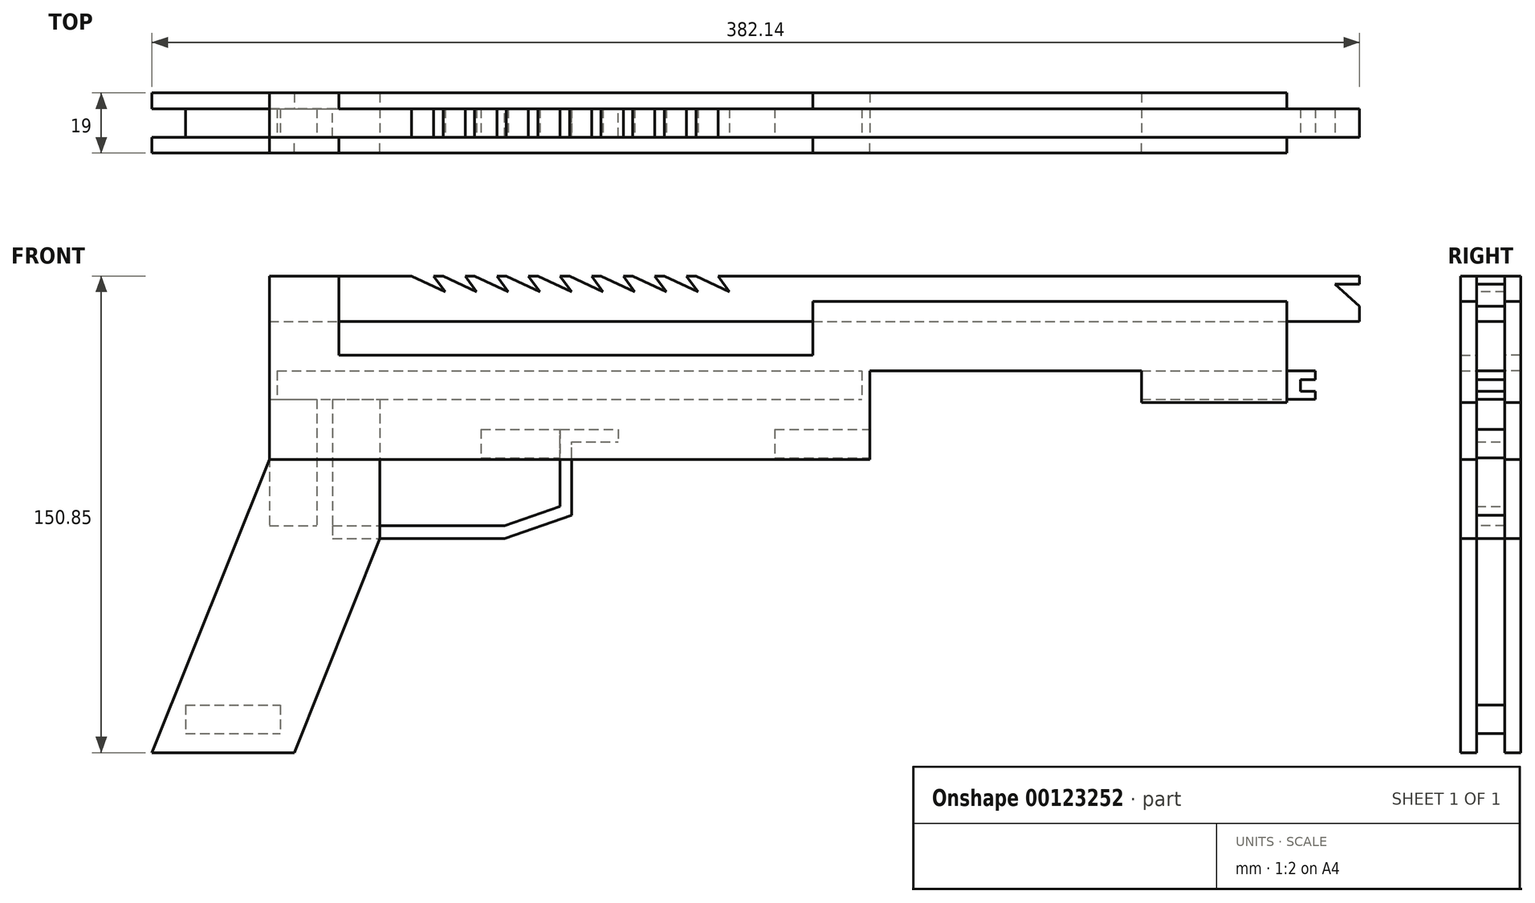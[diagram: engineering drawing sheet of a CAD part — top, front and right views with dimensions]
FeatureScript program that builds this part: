
annotation { "Feature Type Name" : "Feature", "Feature Type Description" : "" }
export const myFeature = defineFeature(function(context is Context, id is Id, definition is map)
    precondition{}
    {
        {
            var Q0;
            Q0=qCreatedBy(makeId("Front.planeOp"),FACE);
            cPlane(context, id + "F0", {"entities" : qUnion([Q0]), "cplaneType" : CPlaneType.OFFSET, "offset" : 4.5 * mm, "oppositeDirection" : true, "width" : 150 * mm, "height" : 150 * mm});
        }
        {
            var Q0;
            Q0=qCreatedBy(id+"F0.planeOp",FACE);
            var sketch = newSketch(context, id + "F1", { "sketchPlane" : qUnion([Q0])});
            skLineSegment(sketch, "E0", {"start": v(0, 0) * mm, "end": v(22, 0) * mm});
            skLineSegment(sketch, "E1", {"start": v(22, 0) * mm, "end": v(22, -25) * mm});
            skLineSegment(sketch, "E2", {"start": v(22, -25) * mm, "end": v(172, -25) * mm});
            skLineSegment(sketch, "E3", {"start": v(172, -25) * mm, "end": v(172, -8) * mm});
            skLineSegment(sketch, "E4", {"start": v(172, -8) * mm, "end": v(322, -8) * mm});
            skLineSegment(sketch, "E5", {"start": v(322, -8) * mm, "end": v(322, -40) * mm});
            skLineSegment(sketch, "E6", {"start": v(322, -40) * mm, "end": v(276, -40) * mm});
            skLineSegment(sketch, "E7", {"start": v(276, -40) * mm, "end": v(276, -30) * mm});
            skLineSegment(sketch, "E8", {"start": v(276, -30) * mm, "end": v(190, -30) * mm});
            skLineSegment(sketch, "E9", {"start": v(190, -30) * mm, "end": v(190, -58) * mm});
            skLineSegment(sketch, "E10", {"start": v(190, -58) * mm, "end": v(0, -58) * mm});
            skLineSegment(sketch, "E11", {"start": v(0, -58) * mm, "end": v(0, 0) * mm});
            skSolve(sketch);
        }
        {
            var Q0;
            Q0=makeQuery(id+"F1.imprint","IMPRINT",FACE,{"disambiguationData":[TD([[makeQuery(id+"F1.imprint","IMPRINT",EDGE,{"derivedFrom":sQuery(id+"F1.wireOp",EDGE,"E0")}),-1.0]])]});
            extrude(context, id + "F2", {"entities" : qUnion([Q0]), "oppositeDirection" : true, "depth" : 5 * mm});
        }
        {
            var Q0;
            Q0=qCreatedBy(makeId("Front.planeOp"),FACE);
            var sketch = newSketch(context, id + "F3", { "sketchPlane" : qUnion([Q0])});
            skLineSegment(sketch, "E12.bottom", {"start": v(2.5, -30) * mm, "end": v(187.5, -30) * mm});
            skLineSegment(sketch, "E12.top", {"start": v(2.5, -39) * mm, "end": v(187.5, -39) * mm});
            skLineSegment(sketch, "E12.left", {"start": v(2.5, -30) * mm, "end": v(2.5, -39) * mm});
            skLineSegment(sketch, "E12.right", {"start": v(187.5, -30) * mm, "end": v(187.5, -39) * mm});
            skLineSegment(sketch, "E13.bottom", {"start": v(276, -30) * mm, "end": v(331, -30) * mm});
            skLineSegment(sketch, "E13.top", {"start": v(276, -39) * mm, "end": v(331, -39) * mm});
            skLineSegment(sketch, "E13.left", {"start": v(276, -30) * mm, "end": v(276, -39) * mm});
            skLineSegment(sketch, "E13.right", {"start": v(331, -30) * mm, "end": v(331, -32.76) * mm});
            skLineSegment(sketch, "E14", {"start": v(331, -32.76) * mm, "end": v(326.28, -32.76) * mm});
            skLineSegment(sketch, "E15", {"start": v(326.28, -32.76) * mm, "end": v(326.28, -36.44) * mm});
            skLineSegment(sketch, "E16", {"start": v(326.28, -36.44) * mm, "end": v(331, -36.44) * mm});
            skLineSegment(sketch, "E17.trimOffspring", {"start": v(331, -36.44) * mm, "end": v(331, -39) * mm});
            skSolve(sketch);
        }
        {
            var Q0;
            Q0 = qSketchRegion(id + "F3", true);
            extrude(context, id + "F4", {"entities" : qUnion([Q0]), "operationType" : NewBodyOperationType.ADD, "endBound" : BoundingType.SYMMETRIC, "oppositeDirection" : true, "depth" : 9 * mm});
        }
        {
            var Q0;
            Q0=qCreatedBy(makeId("Front.planeOp"),FACE);
            var sketch = newSketch(context, id + "F5", { "sketchPlane" : qUnion([Q0])});
            skLineSegment(sketch, "E18.bottom", {"start": v(0, 0) * mm, "end": v(45, 0) * mm});
            skLineSegment(sketch, "E18.top", {"start": v(41.55, -5) * mm, "end": v(41.69, -5) * mm});
            skLineSegment(sketch, "E18.left", {"start": v(0, 0) * mm, "end": v(0, -5) * mm});
            skLineSegment(sketch, "E19.bottom", {"start": v(40.03, 0) * mm, "end": v(39.9, 0) * mm});
            skLineSegment(sketch, "E19.top", {"start": v(41.69, -5) * mm, "end": v(41.55, -5) * mm});
            skLineSegment(sketch, "E20.bottom", {"start": v(55, 0) * mm, "end": v(52.02, 0) * mm});
            skLineSegment(sketch, "E21", {"start": v(45, 0) * mm, "end": v(55.63, -5) * mm});
            skLineSegment(sketch, "E22", {"start": v(55.63, -5) * mm, "end": v(52.02, 0) * mm});
            skLineSegment(sketch, "E23", {"start": v(52.02, 0) * mm, "end": v(55, 0) * mm});
            skLineSegment(sketch, "E24.1.0.0", {"start": v(55, 0) * mm, "end": v(65.63, -5) * mm});
            skLineSegment(sketch, "E24.1.0.1", {"start": v(65.63, -5) * mm, "end": v(62.02, 0) * mm});
            skLineSegment(sketch, "E24.2.0.0", {"start": v(65, 0) * mm, "end": v(75.63, -5) * mm});
            skLineSegment(sketch, "E24.2.0.1", {"start": v(75.63, -5) * mm, "end": v(72.02, 0) * mm});
            skLineSegment(sketch, "E24.3.0.0", {"start": v(75, 0) * mm, "end": v(85.63, -5) * mm});
            skLineSegment(sketch, "E24.3.0.1", {"start": v(85.63, -5) * mm, "end": v(82.02, 0) * mm});
            skLineSegment(sketch, "E24.4.0.0", {"start": v(85, 0) * mm, "end": v(95.63, -5) * mm});
            skLineSegment(sketch, "E24.4.0.1", {"start": v(95.63, -5) * mm, "end": v(92.02, 0) * mm});
            skLineSegment(sketch, "E24.5.0.0", {"start": v(95, 0) * mm, "end": v(105.63, -5) * mm});
            skLineSegment(sketch, "E24.5.0.1", {"start": v(105.63, -5) * mm, "end": v(102.02, 0) * mm});
            skLineSegment(sketch, "E24.6.0.0", {"start": v(105, 0) * mm, "end": v(115.63, -5) * mm});
            skLineSegment(sketch, "E24.6.0.1", {"start": v(115.63, -5) * mm, "end": v(112.02, 0) * mm});
            skLineSegment(sketch, "E24.7.0.0", {"start": v(115, 0) * mm, "end": v(125.63, -5) * mm});
            skLineSegment(sketch, "E24.7.0.1", {"start": v(125.63, -5) * mm, "end": v(122.02, 0) * mm});
            skLineSegment(sketch, "E24.8.0.0", {"start": v(125, 0) * mm, "end": v(135.63, -5) * mm});
            skLineSegment(sketch, "E24.8.0.1", {"start": v(135.63, -5) * mm, "end": v(132.02, 0) * mm});
            skLineSegment(sketch, "E24.9.0.0", {"start": v(135, 0) * mm, "end": v(145.63, -5) * mm});
            skLineSegment(sketch, "E24.9.0.1", {"start": v(145.63, -5) * mm, "end": v(142.02, 0) * mm});
            skLineSegment(sketch, "E24.direction1", {"start": v(45, 0) * mm, "end": v(55, 0) * mm, "construction": true});
            skLineSegment(sketch, "E25.trimOffspring", {"start": v(62.02, 0) * mm, "end": v(65, 0) * mm});
            skLineSegment(sketch, "E26.trimOffspring", {"start": v(72.02, 0) * mm, "end": v(75, 0) * mm});
            skLineSegment(sketch, "E27.trimOffspring", {"start": v(82.02, 0) * mm, "end": v(85, 0) * mm});
            skLineSegment(sketch, "E28.trimOffspring", {"start": v(92.02, 0) * mm, "end": v(95, 0) * mm});
            skLineSegment(sketch, "E29.trimOffspring", {"start": v(102.02, 0) * mm, "end": v(105, 0) * mm});
            skLineSegment(sketch, "E30.trimOffspring", {"start": v(112.02, 0) * mm, "end": v(115, 0) * mm});
            skLineSegment(sketch, "E31.trimOffspring", {"start": v(122.02, 0) * mm, "end": v(125, 0) * mm});
            skLineSegment(sketch, "E32.trimOffspring", {"start": v(132.02, 0) * mm, "end": v(135, 0) * mm});
            skLineSegment(sketch, "E33.trimOffspring", {"start": v(142.02, 0) * mm, "end": v(345, 0) * mm});
            skLineSegment(sketch, "E34", {"start": v(0, -5) * mm, "end": v(0, -14.32) * mm});
            skLineSegment(sketch, "E35", {"start": v(0, -14.32) * mm, "end": v(345, -14.32) * mm});
            skPoint(sketch, "E36.orphan", {"position": v(45, -5) * mm});
            skPoint(sketch, "E37.start.orphan", {"position": v(345, -5) * mm});
            skLineSegment(sketch, "E38", {"start": v(345, 0) * mm, "end": v(345, -2.6) * mm});
            skLineSegment(sketch, "E39", {"start": v(345, -2.6) * mm, "end": v(337.2, -2.6) * mm});
            skLineSegment(sketch, "E40", {"start": v(337.2, -2.6) * mm, "end": v(345, -9.58) * mm});
            skLineSegment(sketch, "E41", {"start": v(345, -9.58) * mm, "end": v(345, -14.32) * mm});
            skSolve(sketch);
        }
        {
            var Q0;
            Q0 = qSketchRegion(id + "F5", true);
            extrude(context, id + "F6", {"entities" : qUnion([Q0]), "operationType" : NewBodyOperationType.ADD, "endBound" : BoundingType.SYMMETRIC, "oppositeDirection" : true, "depth" : 9 * mm});
        }
        {
            var Q0;
            Q0=qCreatedBy(id+"F0.planeOp",FACE);
            var sketch = newSketch(context, id + "F7", { "sketchPlane" : qUnion([Q0])});
            skLineSegment(sketch, "E42", {"start": v(0, -58) * mm, "end": v(35, -58) * mm});
            skLineSegment(sketch, "E43", {"start": v(35, -58) * mm, "end": v(35, -83) * mm});
            skLineSegment(sketch, "E44", {"start": v(35, -83) * mm, "end": v(7.86, -150.85) * mm});
            skLineSegment(sketch, "E45", {"start": v(7.86, -150.85) * mm, "end": v(-37.14, -150.85) * mm});
            skLineSegment(sketch, "E46", {"start": v(-37.14, -150.85) * mm, "end": v(0, -58) * mm});
            skSolve(sketch);
        }
        {
            var Q0;
            Q0=makeQuery(id+"F7.imprint","IMPRINT",FACE,{"disambiguationData":[TD([[makeQuery(id+"F7.imprint","IMPRINT",EDGE,{"derivedFrom":sQuery(id+"F7.wireOp",EDGE,"E42")}),-1.0]])]});
            extrude(context, id + "F8", {"entities" : qUnion([Q0]), "oppositeDirection" : true, "depth" : 5 * mm});
        }
        {
            var Q0;
            Q0=qCreatedBy(makeId("Front.planeOp"),FACE);
            var sketch = newSketch(context, id + "F9", { "sketchPlane" : qUnion([Q0])});
            skLineSegment(sketch, "E47.bottom", {"start": v(0, -39) * mm, "end": v(15, -39) * mm});
            skLineSegment(sketch, "E47.top", {"start": v(0, -79) * mm, "end": v(15, -79) * mm});
            skLineSegment(sketch, "E47.left", {"start": v(0, -39) * mm, "end": v(0, -79) * mm});
            skLineSegment(sketch, "E47.right", {"start": v(15, -39) * mm, "end": v(15, -79) * mm});
            skLineSegment(sketch, "E48.bottom", {"start": v(20, -39) * mm, "end": v(35, -39) * mm});
            skLineSegment(sketch, "E48.top", {"start": v(20, -79) * mm, "end": v(35, -79) * mm});
            skLineSegment(sketch, "E48.left", {"start": v(20, -39) * mm, "end": v(20, -79) * mm});
            skLineSegment(sketch, "E48.right", {"start": v(35, -39) * mm, "end": v(35, -79) * mm});
            skLineSegment(sketch, "E49.bottom", {"start": v(-26.51, -135.79) * mm, "end": v(3.49, -135.79) * mm});
            skLineSegment(sketch, "E49.top", {"start": v(-26.51, -144.79) * mm, "end": v(3.49, -144.79) * mm});
            skLineSegment(sketch, "E49.left", {"start": v(-26.51, -135.79) * mm, "end": v(-26.51, -144.79) * mm});
            skLineSegment(sketch, "E49.right", {"start": v(3.49, -135.79) * mm, "end": v(3.49, -144.79) * mm});
            skLineSegment(sketch, "E50.bottom", {"start": v(160, -48.5) * mm, "end": v(190, -48.5) * mm});
            skLineSegment(sketch, "E50.top", {"start": v(160, -57.5) * mm, "end": v(190, -57.5) * mm});
            skLineSegment(sketch, "E50.left", {"start": v(160, -48.5) * mm, "end": v(160, -57.5) * mm});
            skLineSegment(sketch, "E50.right", {"start": v(190, -48.5) * mm, "end": v(190, -57.5) * mm});
            skLineSegment(sketch, "E51.bottom", {"start": v(67, -48.5) * mm, "end": v(92, -48.5) * mm});
            skLineSegment(sketch, "E51.top", {"start": v(67, -57.5) * mm, "end": v(92, -57.5) * mm});
            skLineSegment(sketch, "E51.left", {"start": v(67, -48.5) * mm, "end": v(67, -57.5) * mm});
            skLineSegment(sketch, "E51.right", {"start": v(92, -48.5) * mm, "end": v(92, -57.5) * mm});
            skSolve(sketch);
        }
        {
            var Q0;
            Q0 = qSketchRegion(id + "F9", true);
            extrude(context, id + "F10", {"entities" : qUnion([Q0]), "endBound" : BoundingType.SYMMETRIC, "oppositeDirection" : true, "depth" : 9 * mm});
        }
        {
            var Q0;
            Q0=makeQuery(id+"F8.opExtrude","SWEPT_BODY",BODY,{"disambiguationData":[OSD([sQuery(id+"F7.wireOp",EDGE,"E42"),sQuery(id+"F7.wireOp",EDGE,"E43"),sQuery(id+"F7.wireOp",EDGE,"E44"),sQuery(id+"F7.wireOp",EDGE,"E45"),sQuery(id+"F7.wireOp",EDGE,"E46")])]});
            var Q1;
            Q1=qCreatedBy(makeId("Front.planeOp"),FACE);
            mirror(context, id + "F11", {"entities" : qUnion([Q0]), "mirrorPlane" : qUnion([Q1])});
        }
        {
            var Q0;
            Q0=qCreatedBy(makeId("Front.planeOp"),FACE);
            cPlane(context, id + "F12", {"entities" : qUnion([Q0]), "cplaneType" : CPlaneType.OFFSET, "offset" : 4.5 * mm, "width" : 150 * mm, "height" : 150 * mm});
        }
        {
            var Q0;
            Q0=qCreatedBy(id+"F12.planeOp",FACE);
            var sketch = newSketch(context, id + "F13", { "sketchPlane" : qUnion([Q0])});
            skLineSegment(sketch, "E52", {"start": v(0, 0) * mm, "end": v(22, 0) * mm});
            skLineSegment(sketch, "E53", {"start": v(22, 0) * mm, "end": v(22, -25) * mm});
            skLineSegment(sketch, "E54", {"start": v(22, -25) * mm, "end": v(172, -25) * mm});
            skLineSegment(sketch, "E55", {"start": v(172, -25) * mm, "end": v(172, -8) * mm});
            skLineSegment(sketch, "E56", {"start": v(172, -8) * mm, "end": v(322, -8) * mm});
            skLineSegment(sketch, "E57", {"start": v(322, -8) * mm, "end": v(322, -40) * mm});
            skLineSegment(sketch, "E58", {"start": v(322, -40) * mm, "end": v(276, -40) * mm});
            skLineSegment(sketch, "E59", {"start": v(276, -40) * mm, "end": v(276, -30) * mm});
            skLineSegment(sketch, "E60", {"start": v(276, -30) * mm, "end": v(190, -30) * mm});
            skLineSegment(sketch, "E61", {"start": v(190, -30) * mm, "end": v(190, -58) * mm});
            skLineSegment(sketch, "E62", {"start": v(190, -58) * mm, "end": v(0, -58) * mm});
            skLineSegment(sketch, "E63", {"start": v(0, -58) * mm, "end": v(0, 0) * mm});
            skSolve(sketch);
        }
        {
            var Q0;
            Q0 = qSketchRegion(id + "F13", true);
            extrude(context, id + "F14", {"entities" : qUnion([Q0]), "depth" : 5 * mm});
        }
        {
            var Q0;
            Q0=qCreatedBy(makeId("Front.planeOp"),FACE);
            var sketch = newSketch(context, id + "F15", { "sketchPlane" : qUnion([Q0])});
            skLineSegment(sketch, "E64", {"start": v(20, -79) * mm, "end": v(74.45, -79) * mm});
            skLineSegment(sketch, "E65", {"start": v(92, -48.5) * mm, "end": v(110.46, -48.5) * mm});
            skLineSegment(sketch, "E66.0", {"start": v(95.68, -52.5) * mm, "end": v(110.46, -52.5) * mm});
            skLineSegment(sketch, "E66.3", {"start": v(20, -83) * mm, "end": v(74.45, -83) * mm});
            skLineSegment(sketch, "E67", {"start": v(110.46, -48.5) * mm, "end": v(110.46, -52.5) * mm});
            skLineSegment(sketch, "E68", {"start": v(20, -79) * mm, "end": v(20, -83) * mm});
            skLineSegment(sketch, "E69", {"start": v(74.45, -79) * mm, "end": v(92, -72.93) * mm});
            skLineSegment(sketch, "E70", {"start": v(74.45, -83) * mm, "end": v(95.68, -75.66) * mm});
            skLineSegment(sketch, "E71.trimOffspring", {"start": v(92, -72.93) * mm, "end": v(92, -48.5) * mm});
            skLineSegment(sketch, "E72.trimOffspring", {"start": v(95.68, -75.66) * mm, "end": v(95.68, -52.5) * mm});
            skSolve(sketch);
        }
        {
            var Q0;
            Q0=makeQuery(id+"F15.imprint","IMPRINT",FACE,{"disambiguationData":[TD([[makeQuery(id+"F15.imprint","IMPRINT",EDGE,{"derivedFrom":sQuery(id+"F15.wireOp",EDGE,"E64")}),-1.0]])]});
            extrude(context, id + "F16", {"entities" : qUnion([Q0]), "endBound" : BoundingType.SYMMETRIC, "depth" : 9 * mm});
        }
    });
